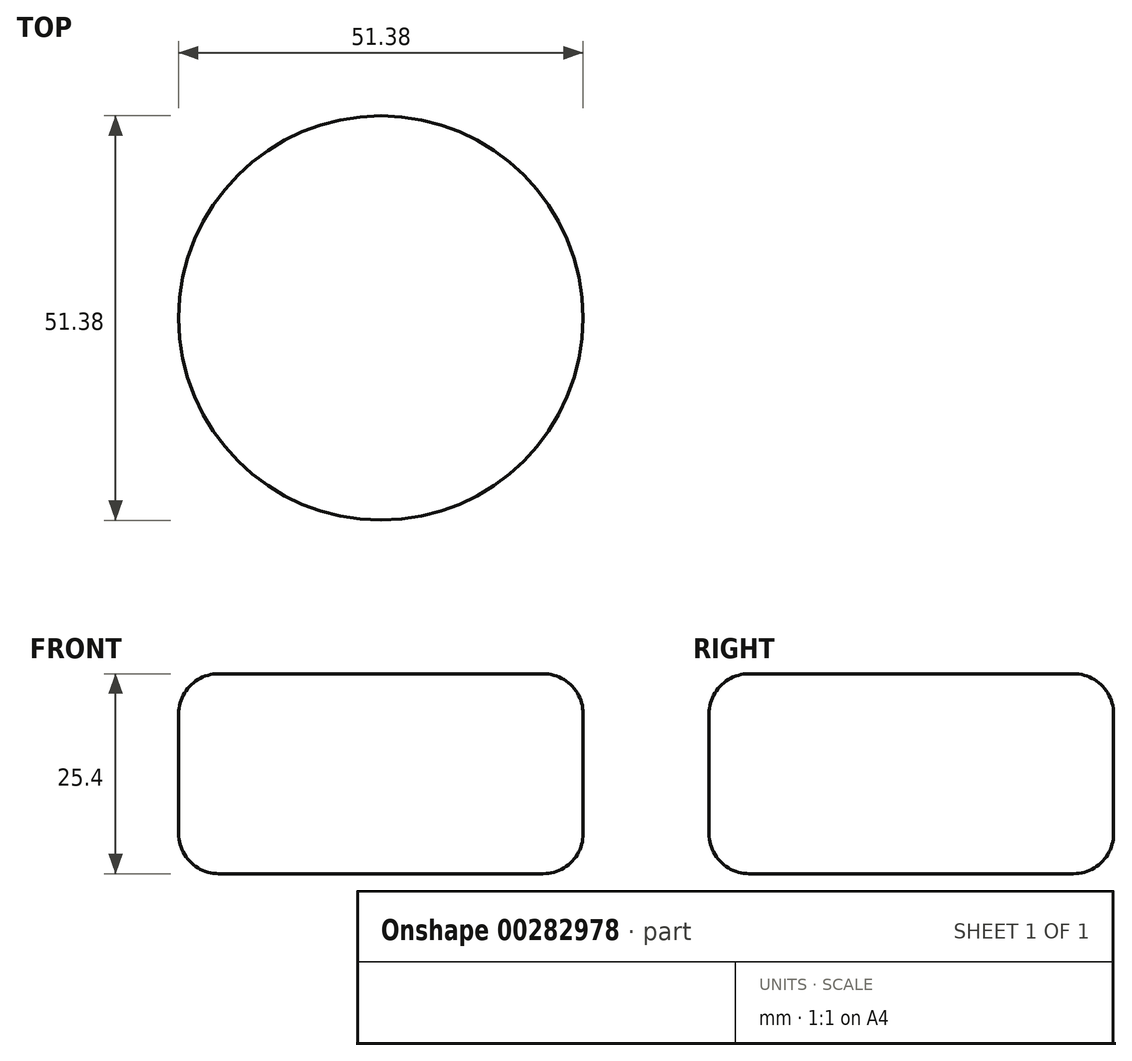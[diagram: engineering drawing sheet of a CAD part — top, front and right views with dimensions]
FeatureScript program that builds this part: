
annotation { "Feature Type Name" : "Feature", "Feature Type Description" : "" }
export const myFeature = defineFeature(function(context is Context, id is Id, definition is map)
    precondition{}
    {
        {
            var Q0;
            Q0=qCreatedBy(makeId("Top.planeOp"),FACE);
            var sketch = newSketch(context, id + "F0", { "sketchPlane" : qUnion([Q0])});
            skCircle(sketch, "E0", {"center": v(0, 0) * mm, "radius": 25.69 * mm});
            skLineSegment(sketch, "E1", {"start": v(-25.69, 0) * mm, "end": v(25.69, 0) * mm});
            skLineSegment(sketch, "E2", {"start": v(0, 0) * mm, "end": v(0, 25.69) * mm});
            skLineSegment(sketch, "E3", {"start": v(0, 0) * mm, "end": v(0, -25.69) * mm});
            skSolve(sketch);
        }
        {
            var Q0;
            {var subQ3=sQuery(id+"F0.wireOp",EDGE,"E2");Q0=makeQuery(id+"F0.imprint","IMPRINT",FACE,{"disambiguationData":[TD([[makeQuery(id+"F0.imprint","IMPRINT",EDGE,{"derivedFrom":subQ3}),-1.0]])]});}
            var Q1;
            {var subQ3=sQuery(id+"F0.wireOp",EDGE,"E3");Q1=makeQuery(id+"F0.imprint","IMPRINT",FACE,{"disambiguationData":[TD([[makeQuery(id+"F0.imprint","IMPRINT",EDGE,{"derivedFrom":subQ3}),1.0]])]});}
            var Q2;
            {var subQ3=sQuery(id+"F0.wireOp",EDGE,"E3");Q2=makeQuery(id+"F0.imprint","IMPRINT",FACE,{"disambiguationData":[TD([[makeQuery(id+"F0.imprint","IMPRINT",EDGE,{"derivedFrom":subQ3}),-1.0]])]});}
            var Q3;
            {var subQ3=sQuery(id+"F0.wireOp",EDGE,"E2");Q3=makeQuery(id+"F0.imprint","IMPRINT",FACE,{"disambiguationData":[TD([[makeQuery(id+"F0.imprint","IMPRINT",EDGE,{"derivedFrom":subQ3}),1.0]])]});}
            extrude(context, id + "F1", {"entities" : qUnion([Q0, Q1, Q2, Q3]), "depth" : 25.4 * mm});
        }
        {
            var Q0;
            Q0=makeQuery(id+"F1.opExtrude","CAP_EDGE",EDGE,{"disambiguationData":[OSD([sQuery(id+"F0.wireOp",EDGE,"E0")])],"isStart":false});
            var Q1;
            Q1=makeQuery(id+"F1.opExtrude","SWEPT_FACE",FACE,{"disambiguationData":[OSD([sQuery(id+"F0.wireOp",EDGE,"E0")])]});
            var Q2;
            Q2=makeQuery(id+"F1.opExtrude","CAP_FACE",FACE,{"disambiguationData":[OSD([sQuery(id+"F0.wireOp",EDGE,"E0")])],"isStart":true});
            fillet(context, id + "F2", {"entities" : qUnion([Q0, Q1, Q2]), "radius" : 5.08 * mm, "tangentPropagation" : true, "allowEdgeOverflow" : false});
        }
    });
